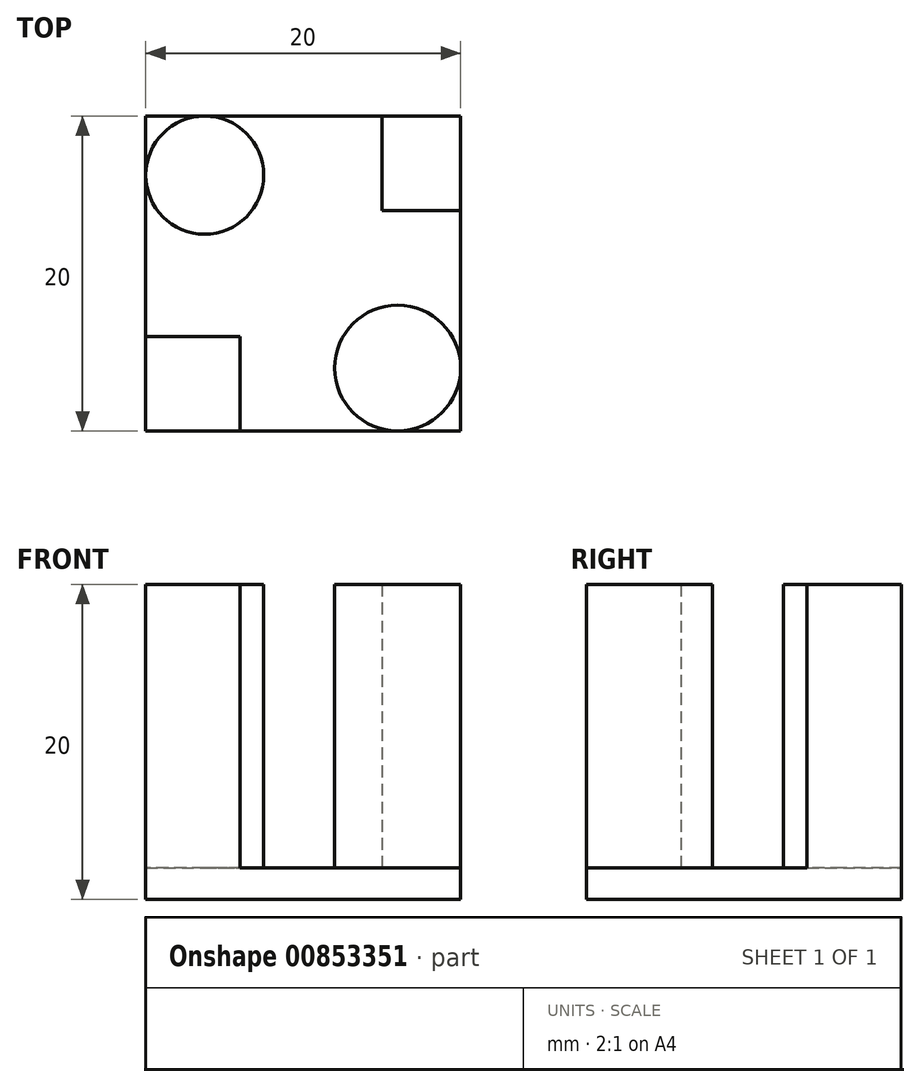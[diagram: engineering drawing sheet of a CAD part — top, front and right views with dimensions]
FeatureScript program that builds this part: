
annotation { "Feature Type Name" : "Feature", "Feature Type Description" : "" }
export const myFeature = defineFeature(function(context is Context, id is Id, definition is map)
    precondition{}
    {
        {
            var Q0;
            Q0=qCreatedBy(makeId("Top.planeOp"),FACE);
            var sketch = newSketch(context, id + "F0", { "sketchPlane" : qUnion([Q0])});
            skLineSegment(sketch, "E0.bottom", {"start": v(-10, 10) * mm, "end": v(10, 10) * mm});
            skLineSegment(sketch, "E0.top", {"start": v(-10, -10) * mm, "end": v(10, -10) * mm});
            skLineSegment(sketch, "E0.left", {"start": v(-10, 10) * mm, "end": v(-10, -10) * mm});
            skLineSegment(sketch, "E0.right", {"start": v(10, 10) * mm, "end": v(10, -10) * mm});
            skSolve(sketch);
        }
        {
            var Q0;
            Q0=makeQuery(id+"F0.imprint","IMPRINT",FACE,{"disambiguationData":[TD([[makeQuery(id+"F0.imprint","IMPRINT",EDGE,{"derivedFrom":sQuery(id+"F0.wireOp",EDGE,"E0.bottom")}),-1.0]])]});
            extrude(context, id + "F1", {"entities" : qUnion([Q0]), "depth" : 2 * mm, "offsetDistance" : 25 * mm});
        }
        {
            var Q0;
            Q0=qCreatedBy(makeId("Top.planeOp"),FACE);
            var sketch = newSketch(context, id + "F2", { "sketchPlane" : qUnion([Q0])});
            skLineSegment(sketch, "E1.bottom", {"start": v(-10, -4) * mm, "end": v(-4, -4) * mm});
            skLineSegment(sketch, "E1.top", {"start": v(-10, -10) * mm, "end": v(-4, -10) * mm});
            skLineSegment(sketch, "E1.left", {"start": v(-10, -4) * mm, "end": v(-10, -10) * mm});
            skLineSegment(sketch, "E1.right", {"start": v(-4, -4) * mm, "end": v(-4, -10) * mm});
            skCircle(sketch, "E2", {"center": v(-6.25, 6.25) * mm, "radius": 3.75 * mm});
            skCircle(sketch, "E3", {"center": v(6, -6) * mm, "radius": 4 * mm});
            skLineSegment(sketch, "E4.bottom", {"start": v(5, 10) * mm, "end": v(10, 10) * mm});
            skLineSegment(sketch, "E4.top", {"start": v(5, 4) * mm, "end": v(10, 4) * mm});
            skLineSegment(sketch, "E4.left", {"start": v(5, 10) * mm, "end": v(5, 4) * mm});
            skLineSegment(sketch, "E4.right", {"start": v(10, 10) * mm, "end": v(10, 4) * mm});
            skSolve(sketch);
        }
        {
            var Q0;
            Q0 = qSketchRegion(id + "F2", true);
            extrude(context, id + "F3", {"entities" : qUnion([Q0]), "operationType" : NewBodyOperationType.ADD, "depth" : 20 * mm, "offsetDistance" : 25 * mm});
        }
    });
